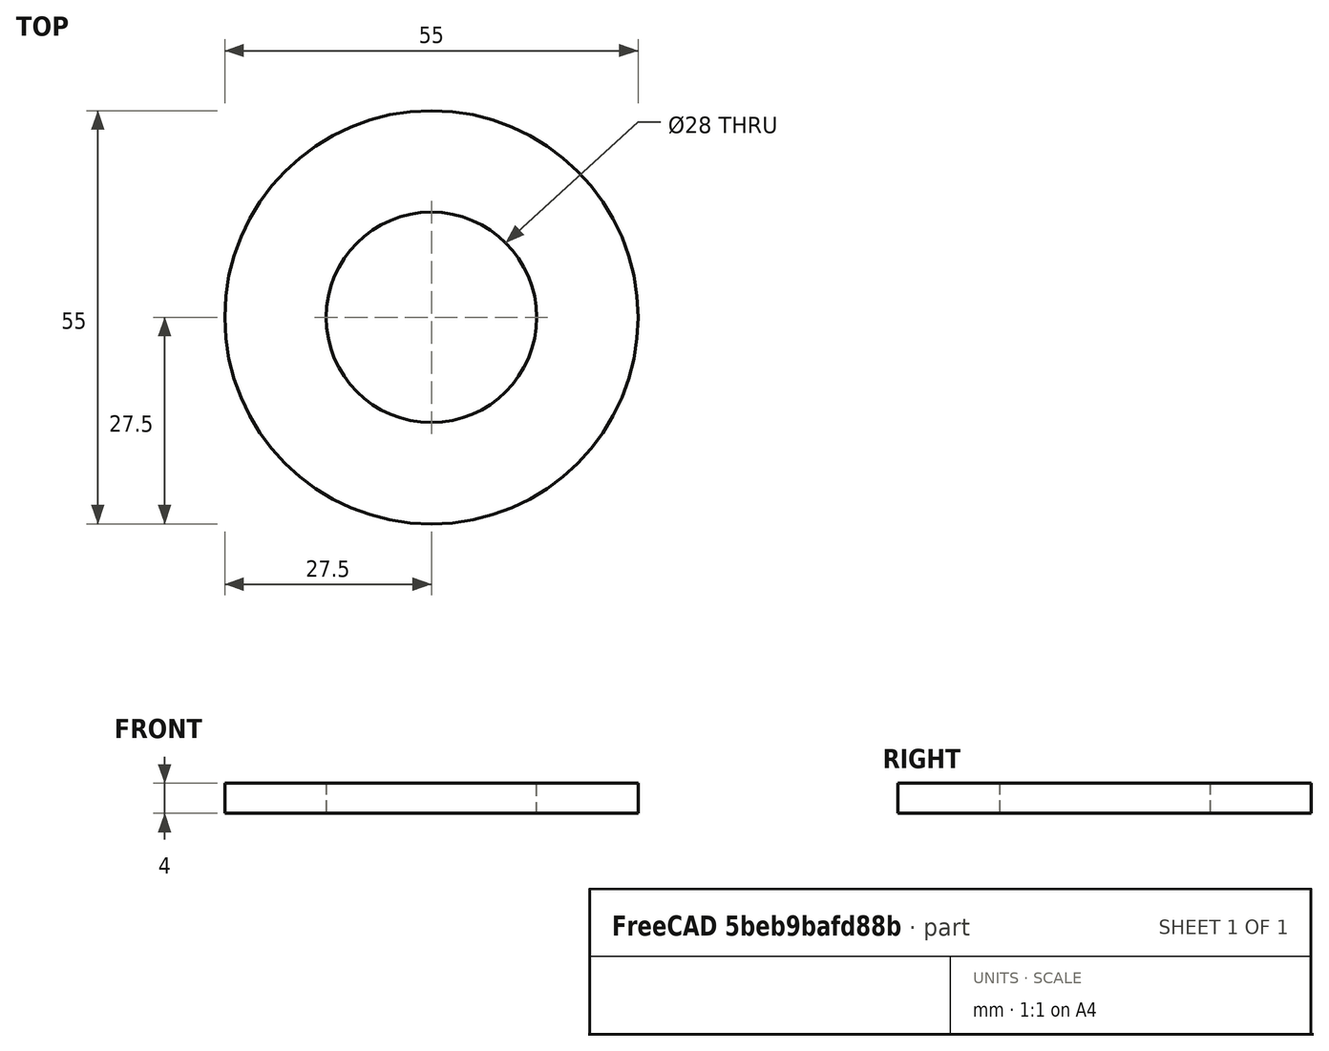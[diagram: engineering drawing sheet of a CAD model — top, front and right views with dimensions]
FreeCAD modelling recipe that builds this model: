
FCSTD DOCUMENT  (FreeCAD 0.19R24276 (Git))
Label: Gear_privod_perehodnik_to_GT2_d28_d55
License: All rights reserved
LicenseURL: http://en.wikipedia.org/wiki/All_rights_reserved
objects: Sketcher::SketchObject×1, PartDesign::Pad×1, PartDesign::Body×1
note: 4 computed .brp shape members not serialized (recipe doc carries the construction recipe); baked Part::Feature solids carry a one-line shape summary decoded from their .brp

FEATURE [Sketcher::SketchObject] Sketch  label="Sketch_d28_d55"
  FullyConstrained = true
  MapMode = 5
  Support = -> [XY_Plane]
  sketch-geometry (2):
    g0: Circle CenterX=0 CenterY=0 CenterZ=0 NormalX=0 NormalY=0 NormalZ=1 AngleXU=0 Radius=14
    g1: Circle CenterX=0 CenterY=0 CenterZ=0 NormalX=0 NormalY=0 NormalZ=1 AngleXU=0 Radius=27.5
  constraints (4):
    c: Coincident(g0,g-1)
    c: Coincident(g1,g0)
    c: Diameter(g0) = 28
    c: Diameter(g1) = 55
FEATURE [PartDesign::Pad] Pad  label="Pad_h4"
  Direction = (1,1,1)
  Length = 4
  Length2 = 100
  Profile = -> Sketch
  Type = 0
FEATURE [PartDesign::Body] Body
  Group = -> [Sketch,Pad]
  Origin = -> Origin
  Tip = -> Pad
